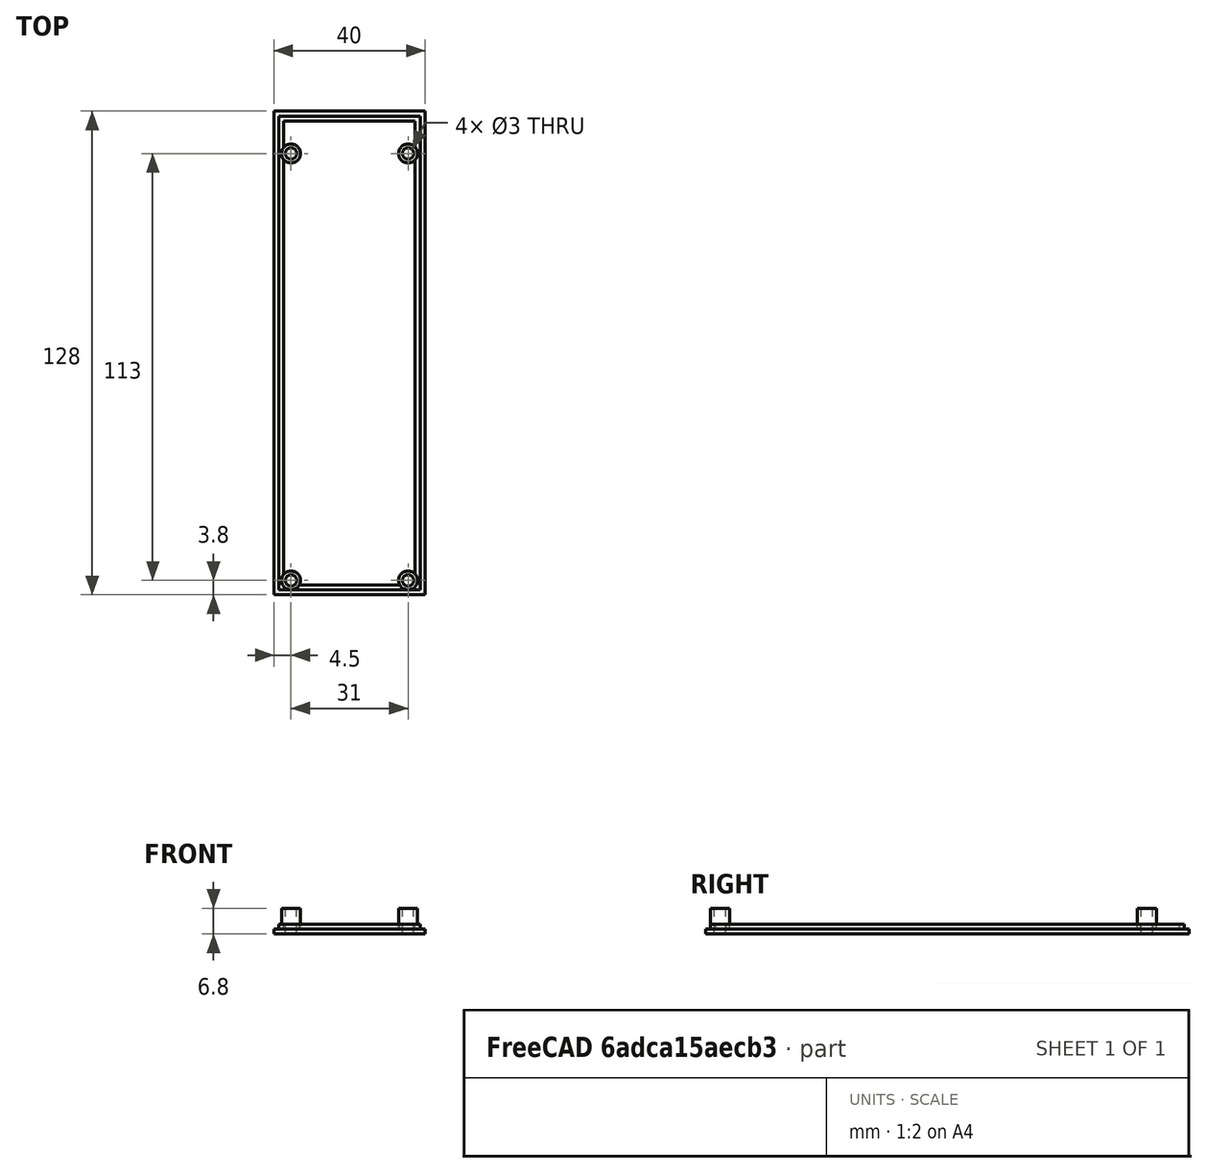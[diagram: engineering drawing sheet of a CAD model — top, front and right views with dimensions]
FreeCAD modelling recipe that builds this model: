
FCSTD DOCUMENT  (FreeCAD 0.18R4 (GitTag))
Label: LCD back-no-supports-v2
License: All rights reserved
LicenseURL: http://en.wikipedia.org/wiki/All_rights_reserved
objects: Part::FeaturePython×6, Part::Box×3, Part::MultiFuse×3, Part::Cut×2, Part::Cylinder×2
note: 16 computed .brp shape members not serialized (recipe doc carries the construction recipe); baked Part::Feature solids carry a one-line shape summary decoded from their .brp

FEATURE [Part::Box] Box  label="Back plate"
  AttacherType = Attacher::AttachEngine3D
  Height = 1.3
  Length = 40
  Width = 128
FEATURE [Part::Box] Box001  label="Wall outer"
  AttacherType = Attacher::AttachEngine3D
  Height = 1.3
  Length = 37.4
  Placement = pos=(1.3,1.3,1.3) rot=(0,0,1;0rad)
  Width = 125.4
FEATURE [Part::Box] Box002  label="Wall cutout"
  AttacherType = Attacher::AttachEngine3D
  Height = 1.3
  Length = 34.8
  Placement = pos=(2.6,2.6,1.3) rot=(0,0,1;0rad)
  Width = 122.8
FEATURE [Part::Cut] Cut  label="Wall"
  Base = -> Box001
  Tool = -> Box002
FEATURE [Part::Cylinder] Cylinder  label="Board post 1"
  Angle = 360
  AttacherType = Attacher::AttachEngine3D
  Height = 6.8
  Placement = pos=(4.5,3.8,0) rot=(0,0,1;0rad)
  Radius = 2.5
FEATURE [Part::FeaturePython] Clone001  label="Board post 3"  # Draft clone (typed FeaturePython)
  AttacherType = Attacher::AttachEngine3D
  Fuse = false
  Objects = -> [Cylinder]
  Placement = pos=(4.5,116.8,0) rot=(0,0,1;0rad)
  Scale = (1,1,1)
FEATURE [Part::FeaturePython] Clone  label="Board post 2"  # Draft clone (typed FeaturePython)
  AttacherType = Attacher::AttachEngine3D
  Fuse = false
  Objects = -> [Cylinder]
  Placement = pos=(35.5,3.8,0) rot=(0,0,1;0rad)
  Scale = (1,1,1)
FEATURE [Part::FeaturePython] Clone002  label="Board post 4"  # Draft clone (typed FeaturePython)
  AttacherType = Attacher::AttachEngine3D
  Fuse = false
  Objects = -> [Cylinder]
  Placement = pos=(35.5,116.8,0) rot=(0,0,1;0rad)
  Scale = (1,1,1)
FEATURE [Part::MultiFuse] Fusion  label="Board posts"
  Shapes = -> [Cylinder,Clone001,Clone,Clone002]
FEATURE [Part::Cylinder] Cylinder001  label="Board post drill 1"
  Angle = 360
  AttacherType = Attacher::AttachEngine3D
  Height = 6.8
  Placement = pos=(4.5,3.8,0) rot=(0,0,1;0rad)
  Radius = 1.5
FEATURE [Part::FeaturePython] Clone003  label="Board post drill 2"  # Draft clone (typed FeaturePython)
  AttacherType = Attacher::AttachEngine3D
  Fuse = false
  Objects = -> [Cylinder001]
  Placement = pos=(35.5,3.8,0) rot=(0,0,1;0rad)
  Scale = (1,1,1)
FEATURE [Part::FeaturePython] Clone004  label="Board post drill 3"  # Draft clone (typed FeaturePython)
  AttacherType = Attacher::AttachEngine3D
  Fuse = false
  Objects = -> [Cylinder001]
  Placement = pos=(4.5,116.8,0) rot=(0,0,1;0rad)
  Scale = (1,1,1)
FEATURE [Part::FeaturePython] Clone005  label="Board post drill 4"  # Draft clone (typed FeaturePython)
  AttacherType = Attacher::AttachEngine3D
  Fuse = false
  Objects = -> [Cylinder001]
  Placement = pos=(35.5,116.8,0) rot=(0,0,1;0rad)
  Scale = (1,1,1)
FEATURE [Part::MultiFuse] Fusion001  label="Board post drills"
  Shapes = -> [Clone005,Cylinder001,Clone003,Clone004]
FEATURE [Part::MultiFuse] Fusion002  label="Plate plus wall and posts"
  Shapes = -> [Box,Fusion,Cut]
FEATURE [Part::Cut] Cut001  label="Back plate plus wall and posts drilled."
  Base = -> Fusion002
  Tool = -> Fusion001
